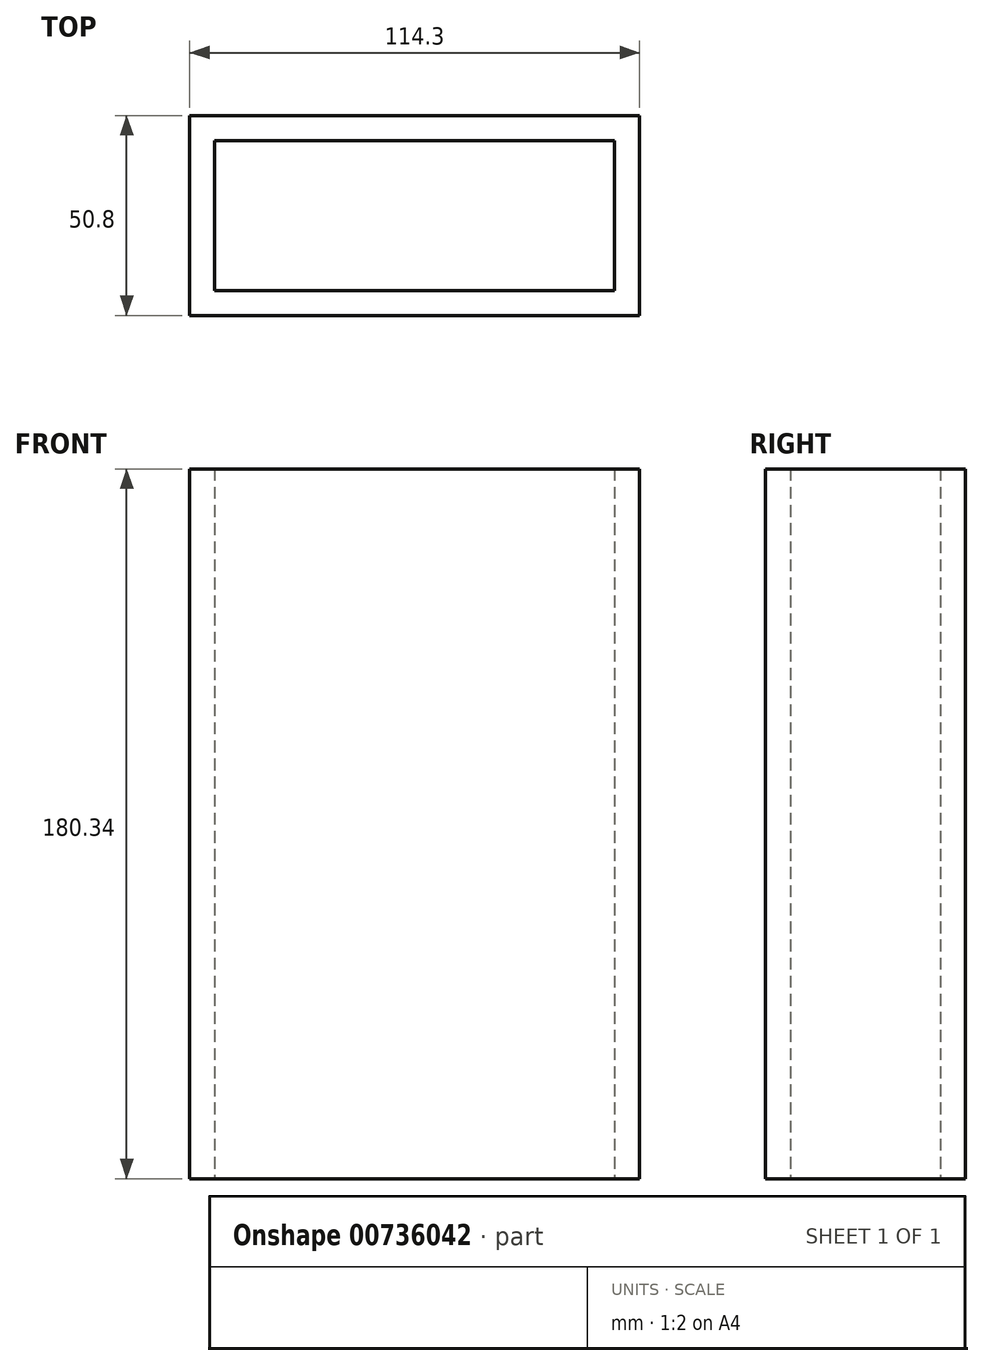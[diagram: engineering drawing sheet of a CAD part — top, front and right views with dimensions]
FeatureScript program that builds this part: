
annotation { "Feature Type Name" : "Feature", "Feature Type Description" : "" }
export const myFeature = defineFeature(function(context is Context, id is Id, definition is map)
    precondition{}
    {
        {
            var Q0;
            Q0=qCreatedBy(makeId("Top.planeOp"),FACE);
            var sketch = newSketch(context, id + "F0", { "sketchPlane" : qUnion([Q0])});
            skLineSegment(sketch, "E0", {"start": v(0, 65.69) * mm, "end": v(0, -56.27) * mm, "construction": true});
            skLineSegment(sketch, "E1", {"start": v(-61.48, 0) * mm, "end": v(53.55, 0) * mm, "construction": true});
            skLineSegment(sketch, "E2.bottom", {"start": v(50.8, 19.05) * mm, "end": v(-50.8, 19.05) * mm});
            skLineSegment(sketch, "E2.top", {"start": v(50.8, -19.05) * mm, "end": v(-50.8, -19.05) * mm});
            skLineSegment(sketch, "E2.left", {"start": v(50.8, 19.05) * mm, "end": v(50.8, -19.05) * mm});
            skLineSegment(sketch, "E2.right", {"start": v(-50.8, 19.05) * mm, "end": v(-50.8, -19.05) * mm});
            skPoint(sketch, "E2.middle", {"position": v(0, 0) * mm});
            skLineSegment(sketch, "E3.0", {"start": v(57.15, 25.4) * mm, "end": v(-57.15, 25.4) * mm});
            skLineSegment(sketch, "E3.1", {"start": v(57.15, 25.4) * mm, "end": v(57.15, -25.4) * mm});
            skLineSegment(sketch, "E3.2", {"start": v(57.15, -25.4) * mm, "end": v(-57.15, -25.4) * mm});
            skLineSegment(sketch, "E3.3", {"start": v(-57.15, 25.4) * mm, "end": v(-57.15, -25.4) * mm});
            skSolve(sketch);
        }
        {
            var Q0;
            Q0 = qSketchRegion(id + "F0", true);
            extrude(context, id + "F1", {"entities" : qUnion([Q0]), "depth" : 180.34 * mm, "offsetDistance" : 25.4 * mm});
        }
    });
